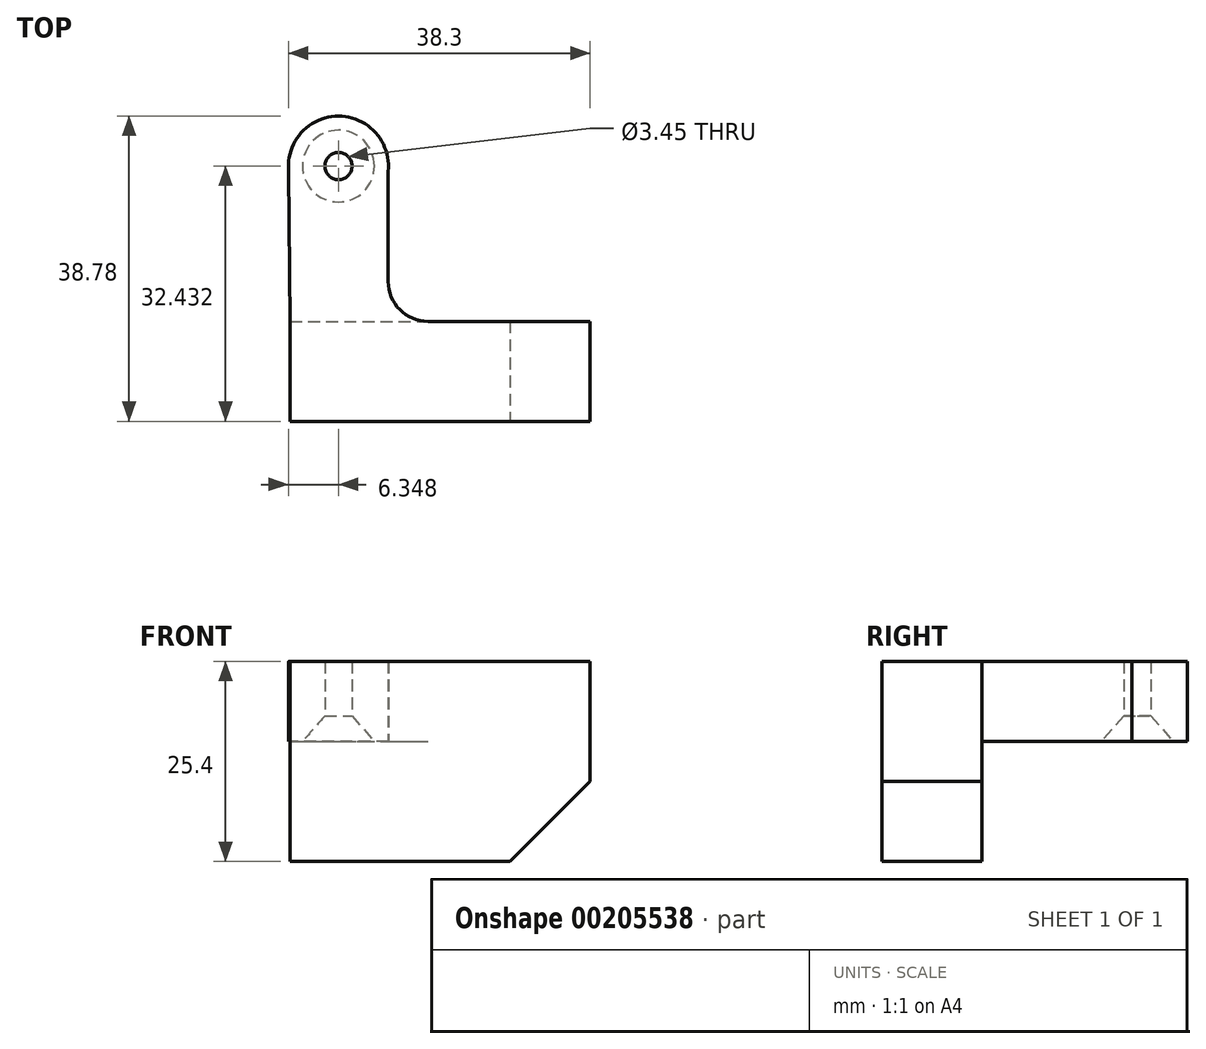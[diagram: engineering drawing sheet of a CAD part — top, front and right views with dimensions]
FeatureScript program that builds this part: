
annotation { "Feature Type Name" : "Feature", "Feature Type Description" : "" }
export const myFeature = defineFeature(function(context is Context, id is Id, definition is map)
    precondition{}
    {
        {
            var Q0;
            Q0=qCreatedBy(makeId("Top.planeOp"),FACE);
            var sketch = newSketch(context, id + "F0", { "sketchPlane" : qUnion([Q0])});
            skLineSegment(sketch, "E0.bottom", {"start": v(-19.97, 6.28) * mm, "end": v(18.13, 6.28) * mm});
            skLineSegment(sketch, "E0.top", {"start": v(-19.97, -6.42) * mm, "end": v(18.13, -6.42) * mm});
            skLineSegment(sketch, "E0.left", {"start": v(-19.97, 6.28) * mm, "end": v(-19.97, -6.42) * mm});
            skLineSegment(sketch, "E0.right", {"start": v(18.13, 6.28) * mm, "end": v(18.13, -6.42) * mm});
            skArc(sketch, "E1", {"start": v(-7.5, 25.33) * mm, "mid": v(-13.82, 32.36) * mm, "end": v(-20.14, 25.33) * mm});
            skPoint(sketch, "E1.second.point", {"position": v(-7.5, 25.33) * mm});
            skPoint(sketch, "E1.third.point", {"position": v(-8.01, 28.58) * mm});
            skLineSegment(sketch, "E2", {"start": v(-20.14, 25.33) * mm, "end": v(-19.97, 6.28) * mm});
            skLineSegment(sketch, "E3", {"start": v(-7.5, 25.33) * mm, "end": v(-7.5, 6.28) * mm});
            skSolve(sketch);
        }
        {
            var Q0;
            Q0=makeQuery(id+"F0.imprint","IMPRINT",FACE,{"disambiguationData":[TD([[makeQuery(id+"F0.imprint","IMPRINT",EDGE,{"derivedFrom":sQuery(id+"F0.wireOp",EDGE,"E0.top")}),1.0]])]});
            var Q1;
            Q1=makeQuery(id+"F0.imprint","IMPRINT",FACE,{"disambiguationData":[TD([[makeQuery(id+"F0.imprint","IMPRINT",EDGE,{"derivedFrom":sQuery(id+"F0.wireOp",EDGE,"E1")}),1.0]])]});
            extrude(context, id + "F1", {"entities" : qUnion([Q0, Q1]), "depth" : 25.4 * mm});
        }
        {
            var Q0;
            Q0=makeQuery(id+"F0.imprint","IMPRINT",FACE,{"disambiguationData":[TD([[makeQuery(id+"F0.imprint","IMPRINT",EDGE,{"derivedFrom":sQuery(id+"F0.wireOp",EDGE,"E1")}),1.0]])]});
            extrude(context, id + "F2", {"entities" : qUnion([Q0]), "operationType" : NewBodyOperationType.REMOVE, "depth" : 15.24 * mm});
        }
        {
            var Q0;
            Q0=sQuery(id+"F0.wireOp",VERTEX,"E1.center");
            var Q1;
            Q1=makeQuery(id+"F1.opExtrude","SWEPT_BODY",BODY,{"disambiguationData":[OSD([sQuery(id+"F0.wireOp",EDGE,"E0.bottom"),sQuery(id+"F0.wireOp",EDGE,"E0.top"),sQuery(id+"F0.wireOp",EDGE,"E0.left"),sQuery(id+"F0.wireOp",EDGE,"E0.right"),sQuery(id+"F0.wireOp",EDGE,"E1"),sQuery(id+"F0.wireOp",EDGE,"E2"),sQuery(id+"F0.wireOp",EDGE,"E3")])]});
            hole(context, id + "F3", {"style" : HoleStyle.C_SINK, "endStyle" : HoleEndStyle.THROUGH, "oppositeDirection" : true, "standardTappedOrClearance" : lookupTablePath({ "standard" : "ANSI", "engagement" : "75%", "pitch" : "32 tpi", "size" : "#8", "type" : "Tapped" }), "standardBlindInLast" : lookupTablePath({ "standard" : "ANSI", "engagement" : "75%", "pitch" : "32 tpi", "size" : "#8", "type" : "Tapped" }), "holeDiameter" : 3.45 * mm, "cSinkDiameter" : 9.12 * mm, "cSinkAngle" : 82 * degree, "locations" : qUnion([Q0]), "scope" : qUnion([Q1]), "isTappedThrough" : true, "majorDiameter" : 4.17 * mm, "showTappedDepth" : true});
        }
        {
            var Q0;
            Q0=makeQuery(id+"F1.opExtrude","SWEPT_EDGE",EDGE,{"disambiguationData":[OSD([sQuery(id+"F0.wireOp",EDGE,"E0.bottom"),sQuery(id+"F0.wireOp",EDGE,"E3")])]});
            fillet(context, id + "F4", {"entities" : qUnion([Q0]), "radius" : 5.08 * mm, "tangentPropagation" : true, "allowEdgeOverflow" : false});
        }
        {
            var Q0;
            Q0=makeQuery(id+"F1.opExtrude","CAP_EDGE",EDGE,{"disambiguationData":[OSD([sQuery(id+"F0.wireOp",EDGE,"E0.right")])],"isStart":true});
            chamfer(context, id + "F5", {"entities" : qUnion([Q0]), "width" : 10.16 * mm, "tangentPropagation" : true});
        }
    });
